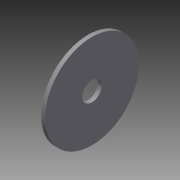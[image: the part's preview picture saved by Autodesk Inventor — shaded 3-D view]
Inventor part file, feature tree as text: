
AUTODESK INVENTOR PART (.ipt)
format: ipt  version: 2015 (Build 190159000, 159)  size: 74,240 bytes
history: native  units: in
note: dims shown in document units (in); Inventor stores cm internally (conversion verified against a paired STEP export)
features: extrude x1, sketch x1
ambient origin geometry x8: Origin, YZ Plane, XZ Plane, XY Plane, X Axis, Y Axis, Z Axis, Center Point
bodies: Solid1 (feature_tree)
feature tree (2):
  extrude  "Extrusion1"  Depth=0.0625in
  sketch  "Sketch1"  dims[d0=0.3125in d1=1.5in d2=0.0625in d3=0.0in]
